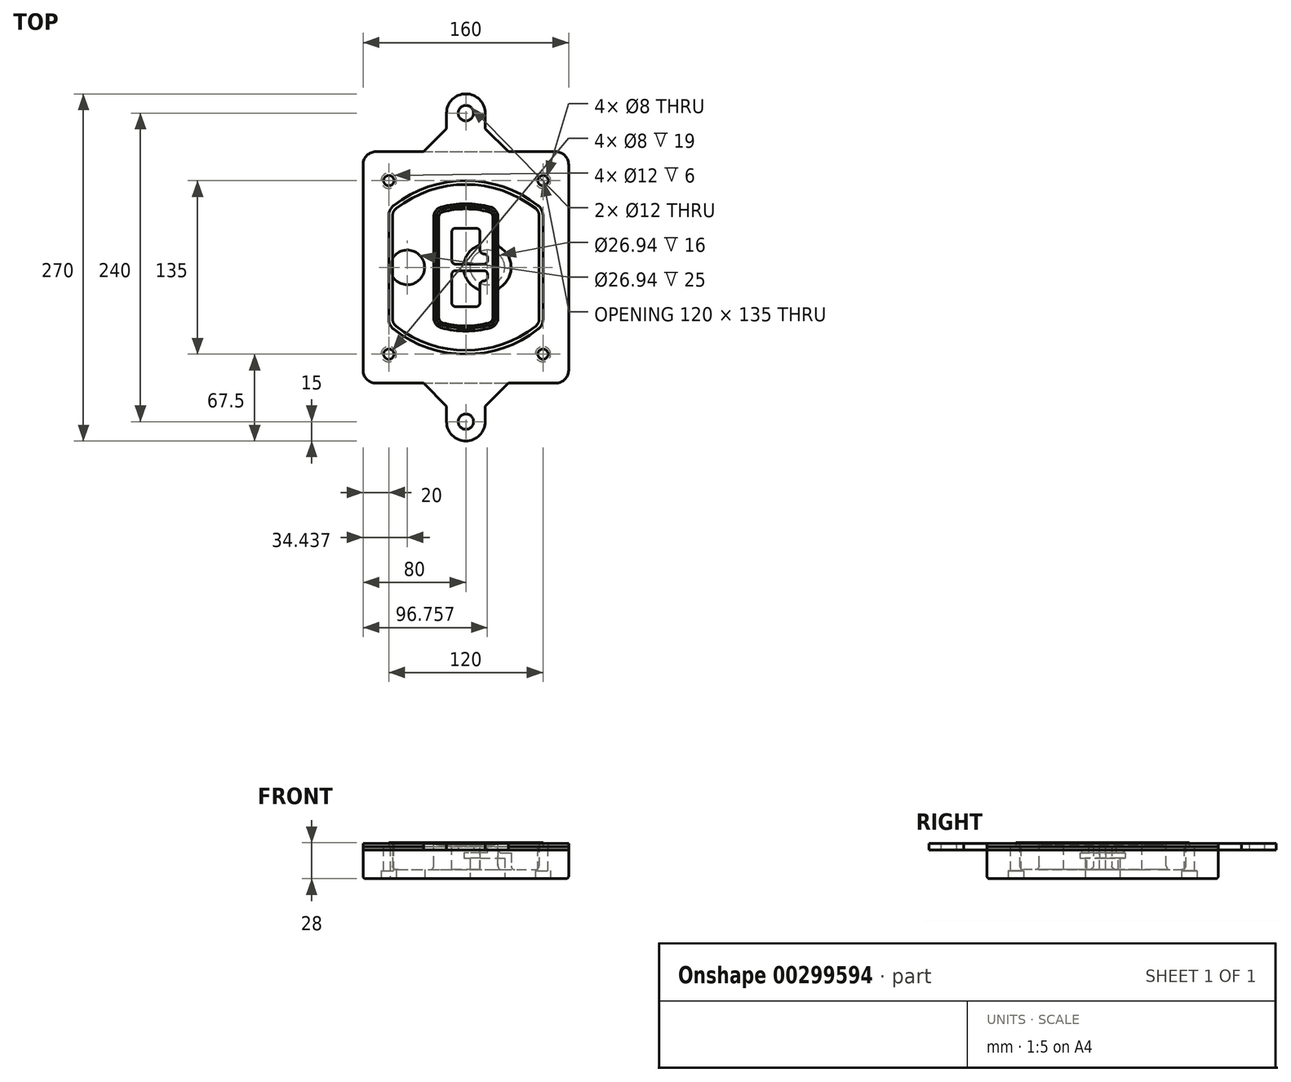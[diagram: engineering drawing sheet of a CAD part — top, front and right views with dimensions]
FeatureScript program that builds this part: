
annotation { "Feature Type Name" : "Feature", "Feature Type Description" : "" }
export const myFeature = defineFeature(function(context is Context, id is Id, definition is map)
    precondition{}
    {
        {
            var Q0;
            Q0=qCreatedBy(makeId("Top.planeOp"),FACE);
            var sketch = newSketch(context, id + "F0", { "sketchPlane" : qUnion([Q0])});
            skPoint(sketch, "E0.rect.middle", {"position": v(0, 0) * mm});
            skLineSegment(sketch, "E1.bottom", {"start": v(-70, -90) * mm, "end": v(70, -90) * mm});
            skLineSegment(sketch, "E1.top", {"start": v(-70, 90) * mm, "end": v(70, 90) * mm});
            skLineSegment(sketch, "E1.left", {"start": v(-80, -80) * mm, "end": v(-80, 80) * mm});
            skLineSegment(sketch, "E1.right", {"start": v(80, -80) * mm, "end": v(80, 80) * mm});
            skLineSegment(sketch, "E2", {"start": v(-80, 90) * mm, "end": v(80, -90) * mm, "construction": true});
            skLineSegment(sketch, "E3", {"start": v(80, 90) * mm, "end": v(-80, -90) * mm, "construction": true});
            skCircle(sketch, "E4", {"center": v(-60, 67.5) * mm, "radius": 4 * mm});
            skCircle(sketch, "E5", {"center": v(60, 67.5) * mm, "radius": 4 * mm});
            skCircle(sketch, "E6", {"center": v(60, -67.5) * mm, "radius": 4 * mm});
            skCircle(sketch, "E7", {"center": v(-60, -67.5) * mm, "radius": 4 * mm});
            skLineSegment(sketch, "E8", {"start": v(-60, 67.5) * mm, "end": v(60, 67.5) * mm, "construction": true});
            skLineSegment(sketch, "E9", {"start": v(60, 67.5) * mm, "end": v(60, -67.5) * mm, "construction": true});
            skLineSegment(sketch, "E10", {"start": v(60, -67.5) * mm, "end": v(-60, -67.5) * mm, "construction": true});
            skLineSegment(sketch, "E11", {"start": v(-60, -67.5) * mm, "end": v(-60, 67.5) * mm, "construction": true});
            skLineSegment(sketch, "E12", {"start": v(-60, 40.3) * mm, "end": v(-60, -40.3) * mm});
            skLineSegment(sketch, "E13", {"start": v(60, 40.3) * mm, "end": v(60, -40.3) * mm});
            skArc(sketch, "E14", {"start": v(56.15, 48.18) * mm, "mid": v(0, 67.5) * mm, "end": v(-56.15, 48.18) * mm});
            skArc(sketch, "E15", {"start": v(-56.15, -48.18) * mm, "mid": v(0, -67.5) * mm, "end": v(56.15, -48.18) * mm});
            skLineSegment(sketch, "E16", {"start": v(-60, 0) * mm, "end": v(60, 0) * mm, "construction": true});
            skPoint(sketch, "E17.visualSharp", {"position": v(-60, -45) * mm});
            skArc(sketch, "E17.filletArc", {"start": v(-60, -40.3) * mm, "mid": v(-58.99, -44.68) * mm, "end": v(-56.15, -48.18) * mm});
            skPoint(sketch, "E18.visualSharp", {"position": v(-60, 45) * mm});
            skArc(sketch, "E18.filletArc", {"start": v(-56.15, 48.18) * mm, "mid": v(-58.99, 44.68) * mm, "end": v(-60, 40.3) * mm});
            skPoint(sketch, "E19.visualSharp", {"position": v(60, 45) * mm});
            skArc(sketch, "E19.filletArc", {"start": v(60, 40.3) * mm, "mid": v(58.99, 44.68) * mm, "end": v(56.15, 48.18) * mm});
            skPoint(sketch, "E20.visualSharp", {"position": v(60, -45) * mm});
            skArc(sketch, "E20.filletArc", {"start": v(56.15, -48.18) * mm, "mid": v(58.99, -44.68) * mm, "end": v(60, -40.3) * mm});
            skPoint(sketch, "E21.visualSharp", {"position": v(-80, 90) * mm});
            skArc(sketch, "E21.filletArc", {"start": v(-70, 90) * mm, "mid": v(-77.07, 87.07) * mm, "end": v(-80, 80) * mm});
            skPoint(sketch, "E22.visualSharp", {"position": v(80, 90) * mm});
            skArc(sketch, "E22.filletArc", {"start": v(80, 80) * mm, "mid": v(77.07, 87.07) * mm, "end": v(70, 90) * mm});
            skPoint(sketch, "E23.visualSharp", {"position": v(80, -90) * mm});
            skArc(sketch, "E23.filletArc", {"start": v(70, -90) * mm, "mid": v(77.07, -87.07) * mm, "end": v(80, -80) * mm});
            skPoint(sketch, "E24.visualSharp", {"position": v(-80, -90) * mm});
            skArc(sketch, "E24.filletArc", {"start": v(-80, -80) * mm, "mid": v(-77.07, -87.07) * mm, "end": v(-70, -90) * mm});
            skArc(sketch, "E25.0", {"start": v(57, 40.3) * mm, "mid": v(56.3, 43.36) * mm, "end": v(54.3, 45.81) * mm});
            skLineSegment(sketch, "E25.1", {"start": v(57, 40.3) * mm, "end": v(57, -40.3) * mm});
            skArc(sketch, "E25.2", {"start": v(54.3, -45.81) * mm, "mid": v(56.3, -43.36) * mm, "end": v(57, -40.3) * mm});
            skArc(sketch, "E25.3", {"start": v(-54.3, -45.81) * mm, "mid": v(0, -64.5) * mm, "end": v(54.3, -45.81) * mm});
            skArc(sketch, "E25.4", {"start": v(-57, -40.3) * mm, "mid": v(-56.3, -43.36) * mm, "end": v(-54.3, -45.81) * mm});
            skArc(sketch, "E25.5", {"start": v(54.3, 45.81) * mm, "mid": v(0, 64.5) * mm, "end": v(-54.3, 45.81) * mm});
            skLineSegment(sketch, "E25.6", {"start": v(-57, 40.3) * mm, "end": v(-57, -40.3) * mm});
            skArc(sketch, "E25.7", {"start": v(-54.3, 45.81) * mm, "mid": v(-56.3, 43.36) * mm, "end": v(-57, 40.3) * mm});
            skArc(sketch, "E26.0", {"start": v(-58.62, 51.33) * mm, "mid": v(-62.58, 46.43) * mm, "end": v(-64, 40.3) * mm});
            skArc(sketch, "E26.1", {"start": v(58.62, 51.33) * mm, "mid": v(0, 71.5) * mm, "end": v(-58.62, 51.33) * mm});
            skArc(sketch, "E26.2", {"start": v(64, 40.3) * mm, "mid": v(62.58, 46.43) * mm, "end": v(58.62, 51.33) * mm});
            skLineSegment(sketch, "E26.3", {"start": v(64, 40.3) * mm, "end": v(64, -40.3) * mm});
            skArc(sketch, "E26.4", {"start": v(58.62, -51.33) * mm, "mid": v(62.58, -46.43) * mm, "end": v(64, -40.3) * mm});
            skLineSegment(sketch, "E26.5", {"start": v(-64, 40.3) * mm, "end": v(-64, -40.3) * mm});
            skArc(sketch, "E26.6", {"start": v(-58.62, -51.33) * mm, "mid": v(0, -71.5) * mm, "end": v(58.62, -51.33) * mm});
            skArc(sketch, "E26.7", {"start": v(-64, -40.3) * mm, "mid": v(-62.58, -46.43) * mm, "end": v(-58.62, -51.33) * mm});
            skSolve(sketch);
        }
        {
            var Q0;
            Q0=makeQuery(id+"F0.imprint","IMPRINT",FACE,{"disambiguationData":[TD([[makeQuery(id+"F0.imprint","IMPRINT",EDGE,{"derivedFrom":sQuery(id+"F0.wireOp",EDGE,"E1.bottom")}),1.0]])]});
            var Q1;
            Q1=makeQuery(id+"F0.imprint","IMPRINT",FACE,{"disambiguationData":[TD([[makeQuery(id+"F0.imprint","IMPRINT",EDGE,{"derivedFrom":sQuery(id+"F0.wireOp",EDGE,"E12")}),1.0]])]});
            var Q2;
            Q2=makeQuery(id+"F0.imprint","IMPRINT",FACE,{"disambiguationData":[TD([[makeQuery(id+"F0.imprint","IMPRINT",EDGE,{"derivedFrom":sQuery(id+"F0.wireOp",EDGE,"E25.0")}),1.0]])]});
            var Q3;
            Q3=makeQuery(id+"F0.imprint","IMPRINT",FACE,{"disambiguationData":[TD([[makeQuery(id+"F0.imprint","IMPRINT",EDGE,{"derivedFrom":sQuery(id+"F0.wireOp",EDGE,"E12")}),-1.0]])]});
            extrude(context, id + "F1", {"entities" : qUnion([Q0, Q1, Q2, Q3]), "oppositeDirection" : true, "depth" : 25 * mm});
        }
        {
            var Q0;
            Q0=makeQuery(id+"F0.imprint","IMPRINT",FACE,{"disambiguationData":[TD([[makeQuery(id+"F0.imprint","IMPRINT",EDGE,{"derivedFrom":sQuery(id+"F0.wireOp",EDGE,"E12")}),1.0]])]});
            extrude(context, id + "F2", {"entities" : qUnion([Q0]), "operationType" : NewBodyOperationType.ADD, "depth" : 3 * mm});
        }
        {
            var Q0;
            Q0=makeQuery(id+"F0.imprint","IMPRINT",FACE,{"disambiguationData":[TD([[makeQuery(id+"F0.imprint","IMPRINT",EDGE,{"derivedFrom":sQuery(id+"F0.wireOp",EDGE,"E25.0")}),1.0]])]});
            extrude(context, id + "F3", {"entities" : qUnion([Q0]), "operationType" : NewBodyOperationType.REMOVE, "oppositeDirection" : true, "depth" : 18 * mm});
        }
        {
            var Q0;
            Q0=makeQuery(id+"F2.opExtrude","CAP_FACE",FACE,{"disambiguationData":[OSD([sQuery(id+"F0.wireOp",EDGE,"E12"),sQuery(id+"F0.wireOp",EDGE,"E13"),sQuery(id+"F0.wireOp",EDGE,"E14"),sQuery(id+"F0.wireOp",EDGE,"E15"),sQuery(id+"F0.wireOp",EDGE,"E17.filletArc"),sQuery(id+"F0.wireOp",EDGE,"E18.filletArc"),sQuery(id+"F0.wireOp",EDGE,"E19.filletArc"),sQuery(id+"F0.wireOp",EDGE,"E20.filletArc"),sQuery(id+"F0.wireOp",EDGE,"E25.0"),sQuery(id+"F0.wireOp",EDGE,"E25.1"),sQuery(id+"F0.wireOp",EDGE,"E25.2"),sQuery(id+"F0.wireOp",EDGE,"E25.3"),sQuery(id+"F0.wireOp",EDGE,"E25.4"),sQuery(id+"F0.wireOp",EDGE,"E25.5"),sQuery(id+"F0.wireOp",EDGE,"E25.6"),sQuery(id+"F0.wireOp",EDGE,"E25.7")])],"isStart":false});
            var sketch = newSketch(context, id + "F4", { "sketchPlane" : qUnion([Q0])});
            skArc(sketch, "E27.0", {"start": v(-19.08, -46.97) * mm, "mid": v(0, -49.5) * mm, "end": v(19.08, -46.97) * mm});
            skArc(sketch, "E28.0", {"start": v(19.08, 46.97) * mm, "mid": v(0, 49.5) * mm, "end": v(-19.08, 46.97) * mm});
            skLineSegment(sketch, "E29", {"start": v(-25, 39.25) * mm, "end": v(-25, -39.25) * mm});
            skLineSegment(sketch, "E30", {"start": v(25, 39.25) * mm, "end": v(25, -39.25) * mm});
            skLineSegment(sketch, "E31", {"start": v(-25, 45.1) * mm, "end": v(25, 45.1) * mm, "construction": true});
            skLineSegment(sketch, "E32", {"start": v(-25, -45.1) * mm, "end": v(25, -45.1) * mm, "construction": true});
            skPoint(sketch, "E33.visualSharp", {"position": v(-25, 45.1) * mm});
            skArc(sketch, "E33.filletArc", {"start": v(-19.08, 46.97) * mm, "mid": v(-23.35, 44.11) * mm, "end": v(-25, 39.25) * mm});
            skPoint(sketch, "E34.visualSharp", {"position": v(25, 45.1) * mm});
            skArc(sketch, "E34.filletArc", {"start": v(25, 39.25) * mm, "mid": v(23.35, 44.11) * mm, "end": v(19.08, 46.97) * mm});
            skPoint(sketch, "E35.visualSharp", {"position": v(25, -45.1) * mm});
            skArc(sketch, "E35.filletArc", {"start": v(19.08, -46.97) * mm, "mid": v(23.35, -44.11) * mm, "end": v(25, -39.25) * mm});
            skPoint(sketch, "E36.visualSharp", {"position": v(-25, -45.1) * mm});
            skArc(sketch, "E36.filletArc", {"start": v(-25, -39.25) * mm, "mid": v(-23.35, -44.11) * mm, "end": v(-19.08, -46.97) * mm});
            skArc(sketch, "E37.0", {"start": v(54.3, 45.81) * mm, "mid": v(0, 64.5) * mm, "end": v(-54.3, 45.81) * mm});
            skArc(sketch, "E37.1", {"start": v(-54.3, 45.81) * mm, "mid": v(-56.3, 43.36) * mm, "end": v(-57, 40.3) * mm});
            skLineSegment(sketch, "E37.2", {"start": v(-57, 40.3) * mm, "end": v(-57, -40.3) * mm});
            skArc(sketch, "E37.3", {"start": v(-57, -40.3) * mm, "mid": v(-56.3, -43.36) * mm, "end": v(-54.3, -45.81) * mm});
            skArc(sketch, "E37.4", {"start": v(-54.3, -45.81) * mm, "mid": v(0, -64.5) * mm, "end": v(54.3, -45.81) * mm});
            skArc(sketch, "E37.5", {"start": v(54.3, -45.81) * mm, "mid": v(56.3, -43.36) * mm, "end": v(57, -40.3) * mm});
            skLineSegment(sketch, "E37.6", {"start": v(57, 40.3) * mm, "end": v(57, -40.3) * mm});
            skArc(sketch, "E37.7", {"start": v(57, 40.3) * mm, "mid": v(56.3, 43.36) * mm, "end": v(54.3, 45.81) * mm});
            skLineSegment(sketch, "E38.0", {"start": v(23, 39.25) * mm, "end": v(23, -39.25) * mm});
            skArc(sketch, "E38.1", {"start": v(18.56, -45.04) * mm, "mid": v(21.76, -42.9) * mm, "end": v(23, -39.25) * mm});
            skArc(sketch, "E38.2", {"start": v(-18.56, -45.04) * mm, "mid": v(0, -47.5) * mm, "end": v(18.56, -45.04) * mm});
            skArc(sketch, "E38.3", {"start": v(-23, -39.25) * mm, "mid": v(-21.76, -42.9) * mm, "end": v(-18.56, -45.04) * mm});
            skLineSegment(sketch, "E38.4", {"start": v(-23, 39.25) * mm, "end": v(-23, -39.25) * mm});
            skArc(sketch, "E38.5", {"start": v(23, 39.25) * mm, "mid": v(21.76, 42.9) * mm, "end": v(18.56, 45.04) * mm});
            skArc(sketch, "E38.6", {"start": v(-18.56, 45.04) * mm, "mid": v(-21.76, 42.9) * mm, "end": v(-23, 39.25) * mm});
            skArc(sketch, "E38.7", {"start": v(18.56, 45.04) * mm, "mid": v(0, 47.5) * mm, "end": v(-18.56, 45.04) * mm});
            skArc(sketch, "E39.0", {"start": v(21, 39.25) * mm, "mid": v(20.18, 41.68) * mm, "end": v(18.04, 43.1) * mm});
            skLineSegment(sketch, "E39.1", {"start": v(21, 39.25) * mm, "end": v(21, -39.25) * mm});
            skArc(sketch, "E39.2", {"start": v(18.04, -43.1) * mm, "mid": v(20.18, -41.68) * mm, "end": v(21, -39.25) * mm});
            skArc(sketch, "E39.3", {"start": v(-18.04, -43.1) * mm, "mid": v(0, -45.5) * mm, "end": v(18.04, -43.1) * mm});
            skArc(sketch, "E39.4", {"start": v(-21, -39.25) * mm, "mid": v(-20.18, -41.68) * mm, "end": v(-18.04, -43.1) * mm});
            skArc(sketch, "E39.5", {"start": v(18.04, 43.1) * mm, "mid": v(0, 45.5) * mm, "end": v(-18.04, 43.1) * mm});
            skLineSegment(sketch, "E39.6", {"start": v(-21, 39.25) * mm, "end": v(-21, -39.25) * mm});
            skArc(sketch, "E39.7", {"start": v(-18.04, 43.1) * mm, "mid": v(-20.18, 41.68) * mm, "end": v(-21, 39.25) * mm});
            skLineSegment(sketch, "E40", {"start": v(-25, 0) * mm, "end": v(25, 0) * mm, "construction": true});
            skLineSegment(sketch, "E41", {"start": v(-11, 5.5) * mm, "end": v(-11, 27.5) * mm});
            skLineSegment(sketch, "E42", {"start": v(-8, 30.5) * mm, "end": v(8, 30.5) * mm});
            skLineSegment(sketch, "E43", {"start": v(11, 27.5) * mm, "end": v(11, 13.5) * mm});
            skLineSegment(sketch, "E44", {"start": v(14, 10.5) * mm, "end": v(14, 10.5) * mm});
            skLineSegment(sketch, "E45", {"start": v(17, 7.5) * mm, "end": v(17, 5.5) * mm});
            skLineSegment(sketch, "E46", {"start": v(14, 2.5) * mm, "end": v(-8, 2.5) * mm});
            skPoint(sketch, "E47.visualSharp", {"position": v(-11, 30.5) * mm});
            skArc(sketch, "E47.filletArc", {"start": v(-8, 30.5) * mm, "mid": v(-10.12, 29.62) * mm, "end": v(-11, 27.5) * mm});
            skPoint(sketch, "E48.visualSharp", {"position": v(11, 30.5) * mm});
            skArc(sketch, "E48.filletArc", {"start": v(11, 27.5) * mm, "mid": v(10.12, 29.62) * mm, "end": v(8, 30.5) * mm});
            skPoint(sketch, "E49.visualSharp", {"position": v(11, 10.5) * mm});
            skArc(sketch, "E49.filletArc", {"start": v(11, 13.5) * mm, "mid": v(11.88, 11.38) * mm, "end": v(14, 10.5) * mm});
            skPoint(sketch, "E50.visualSharp", {"position": v(17, 10.5) * mm});
            skArc(sketch, "E50.filletArc", {"start": v(17, 7.5) * mm, "mid": v(16.12, 9.62) * mm, "end": v(14, 10.5) * mm});
            skPoint(sketch, "E51.visualSharp", {"position": v(17, 2.5) * mm});
            skArc(sketch, "E51.filletArc", {"start": v(14, 2.5) * mm, "mid": v(16.12, 3.38) * mm, "end": v(17, 5.5) * mm});
            skPoint(sketch, "E52.visualSharp", {"position": v(-11, 2.5) * mm});
            skArc(sketch, "E52.filletArc", {"start": v(-11, 5.5) * mm, "mid": v(-10.12, 3.38) * mm, "end": v(-8, 2.5) * mm});
            skLineSegment(sketch, "E53.0.MirrorCS", {"start": v(14, -2.5) * mm, "end": v(-8, -2.5) * mm});
            skArc(sketch, "E54.0.MirrorCS", {"start": v(-11, -5.5) * mm, "mid": v(-10.12, -3.38) * mm, "end": v(-8, -2.5) * mm});
            skLineSegment(sketch, "E55.0.MirrorCS", {"start": v(-11, -5.5) * mm, "end": v(-11, -27.5) * mm});
            skArc(sketch, "E56.0.MirrorCS", {"start": v(-8, -30.5) * mm, "mid": v(-10.12, -29.62) * mm, "end": v(-11, -27.5) * mm});
            skLineSegment(sketch, "E57.0.MirrorCS", {"start": v(-8, -30.5) * mm, "end": v(8, -30.5) * mm});
            skArc(sketch, "E58.0.MirrorCS", {"start": v(11, -27.5) * mm, "mid": v(10.12, -29.62) * mm, "end": v(8, -30.5) * mm});
            skLineSegment(sketch, "E59.0.MirrorCS", {"start": v(11, -27.5) * mm, "end": v(11, -13.5) * mm});
            skArc(sketch, "E60.0.MirrorCS", {"start": v(11, -13.5) * mm, "mid": v(11.88, -11.38) * mm, "end": v(14, -10.5) * mm});
            skArc(sketch, "E61.0.MirrorCS", {"start": v(17, -7.5) * mm, "mid": v(16.12, -9.62) * mm, "end": v(14, -10.5) * mm});
            skLineSegment(sketch, "E62.0.MirrorCS", {"start": v(17, -7.5) * mm, "end": v(17, -5.5) * mm});
            skArc(sketch, "E63.0.MirrorCS", {"start": v(14, -2.5) * mm, "mid": v(16.12, -3.38) * mm, "end": v(17, -5.5) * mm});
            skSolve(sketch);
        }
        {
            var Q0;
            Q0=makeQuery(id+"F4.imprint","IMPRINT",FACE,{"disambiguationData":[TD([[makeQuery(id+"F4.imprint","IMPRINT",EDGE,{"derivedFrom":sQuery(id+"F4.wireOp",EDGE,"E27.0")}),1.0]])]});
            var Q1;
            Q1=makeQuery(id+"F4.imprint","IMPRINT",FACE,{"disambiguationData":[TD([[makeQuery(id+"F4.imprint","IMPRINT",EDGE,{"derivedFrom":sQuery(id+"F4.wireOp",EDGE,"E38.0")}),-1.0]])]});
            var Q2;
            Q2=makeQuery(id+"F4.imprint","IMPRINT",FACE,{"disambiguationData":[TD([[makeQuery(id+"F4.imprint","IMPRINT",EDGE,{"derivedFrom":sQuery(id+"F4.wireOp",EDGE,"E39.0")}),1.0]])]});
            extrude(context, id + "F5", {"entities" : qUnion([Q0, Q1, Q2]), "operationType" : NewBodyOperationType.ADD, "endBound" : BoundingType.UP_TO_NEXT, "oppositeDirection" : true, "depth" : 25 * mm});
        }
        {
            var Q0;
            Q0=makeQuery(id+"F4.imprint","IMPRINT",FACE,{"disambiguationData":[TD([[makeQuery(id+"F4.imprint","IMPRINT",EDGE,{"derivedFrom":sQuery(id+"F4.wireOp",EDGE,"E38.0")}),-1.0]])]});
            extrude(context, id + "F6", {"entities" : qUnion([Q0]), "operationType" : NewBodyOperationType.REMOVE, "oppositeDirection" : true, "depth" : 2 * mm});
        }
        {
            var Q0;
            Q0=makeQuery(id+"F1.opExtrude","CAP_FACE",FACE,{"disambiguationData":[OSD([sQuery(id+"F0.wireOp",EDGE,"E1.bottom"),sQuery(id+"F0.wireOp",EDGE,"E1.top"),sQuery(id+"F0.wireOp",EDGE,"E1.left"),sQuery(id+"F0.wireOp",EDGE,"E1.right"),sQuery(id+"F0.wireOp",EDGE,"E4"),sQuery(id+"F0.wireOp",EDGE,"E5"),sQuery(id+"F0.wireOp",EDGE,"E6"),sQuery(id+"F0.wireOp",EDGE,"E7"),sQuery(id+"F0.wireOp",EDGE,"E21.filletArc"),sQuery(id+"F0.wireOp",EDGE,"E22.filletArc"),sQuery(id+"F0.wireOp",EDGE,"E23.filletArc"),sQuery(id+"F0.wireOp",EDGE,"E24.filletArc")])],"isStart":false});
            var sketch = newSketch(context, id + "F7", { "sketchPlane" : qUnion([Q0])});
            skCircle(sketch, "E64", {"center": v(16.76, 0) * mm, "radius": 13.47 * mm});
            skCircle(sketch, "E65", {"center": v(-45.56, 0) * mm, "radius": 13.47 * mm});
            skLineSegment(sketch, "E66", {"start": v(80, 0) * mm, "end": v(-80, 0) * mm});
            skCircle(sketch, "E67", {"center": v(16.76, 0) * mm, "radius": 18.47 * mm});
            skCircle(sketch, "E68", {"center": v(60, -67.5) * mm, "radius": 6 * mm});
            skCircle(sketch, "E69", {"center": v(-60, -67.5) * mm, "radius": 6 * mm});
            skCircle(sketch, "E70", {"center": v(-60, 67.5) * mm, "radius": 6 * mm});
            skCircle(sketch, "E71", {"center": v(60, 67.5) * mm, "radius": 6 * mm});
            skSolve(sketch);
        }
        {
            var Q0;
            {var subQ1=sQuery(id+"F7.wireOp",EDGE,"E66");var subQ4=sQuery(id+"F7.wireOp",EDGE,"E64");var subQ6=makeQuery(id+"F7.imprint","INTERSECT",VERTEX,{"disambiguationData":[OD(0.0)],"derivedFrom":[subQ4,subQ1]});Q0=makeQuery(id+"F7.imprint","IMPRINT",FACE,{"disambiguationData":[TD([[makeQuery(id+"F7.imprint","IMPRINT",EDGE,{"disambiguationData":[TD([[subQ6,-1.0]])],"derivedFrom":subQ4}),-1.0]])]});}
            var Q1;
            {var subQ0=sQuery(id+"F7.wireOp",EDGE,"E66");var subQ1=sQuery(id+"F7.wireOp",EDGE,"E64");var subQ3=makeQuery(id+"F7.imprint","INTERSECT",VERTEX,{"disambiguationData":[OD(0.0)],"derivedFrom":[subQ1,subQ0]});Q1=makeQuery(id+"F7.imprint","IMPRINT",FACE,{"disambiguationData":[TD([[makeQuery(id+"F7.imprint","IMPRINT",EDGE,{"disambiguationData":[TD([[subQ3,-1.0]])],"derivedFrom":subQ1}),1.0]])]});}
            var Q2;
            {var subQ0=sQuery(id+"F7.wireOp",EDGE,"E66");var subQ1=sQuery(id+"F7.wireOp",EDGE,"E64");var subQ3=makeQuery(id+"F7.imprint","INTERSECT",VERTEX,{"disambiguationData":[OD(0.0)],"derivedFrom":[subQ1,subQ0]});Q2=makeQuery(id+"F7.imprint","IMPRINT",FACE,{"disambiguationData":[TD([[makeQuery(id+"F7.imprint","IMPRINT",EDGE,{"disambiguationData":[TD([[subQ3,1.0]])],"derivedFrom":subQ1}),1.0]])]});}
            var Q3;
            {var subQ1=sQuery(id+"F7.wireOp",EDGE,"E66");var subQ4=sQuery(id+"F7.wireOp",EDGE,"E64");var subQ6=makeQuery(id+"F7.imprint","INTERSECT",VERTEX,{"disambiguationData":[OD(0.0)],"derivedFrom":[subQ4,subQ1]});Q3=makeQuery(id+"F7.imprint","IMPRINT",FACE,{"disambiguationData":[TD([[makeQuery(id+"F7.imprint","IMPRINT",EDGE,{"disambiguationData":[TD([[subQ6,1.0]])],"derivedFrom":subQ4}),-1.0]])]});}
            extrude(context, id + "F8", {"entities" : qUnion([Q0, Q1, Q2, Q3]), "operationType" : NewBodyOperationType.ADD, "oppositeDirection" : true, "depth" : 20 * mm});
        }
        {
            var Q0;
            {var subQ0=sQuery(id+"F7.wireOp",EDGE,"E66");var subQ1=sQuery(id+"F7.wireOp",EDGE,"E64");var subQ3=makeQuery(id+"F7.imprint","INTERSECT",VERTEX,{"disambiguationData":[OD(0.0)],"derivedFrom":[subQ1,subQ0]});Q0=makeQuery(id+"F7.imprint","IMPRINT",FACE,{"disambiguationData":[TD([[makeQuery(id+"F7.imprint","IMPRINT",EDGE,{"disambiguationData":[TD([[subQ3,-1.0]])],"derivedFrom":subQ1}),1.0]])]});}
            var Q1;
            {var subQ0=sQuery(id+"F7.wireOp",EDGE,"E66");var subQ1=sQuery(id+"F7.wireOp",EDGE,"E64");var subQ3=makeQuery(id+"F7.imprint","INTERSECT",VERTEX,{"disambiguationData":[OD(0.0)],"derivedFrom":[subQ1,subQ0]});Q1=makeQuery(id+"F7.imprint","IMPRINT",FACE,{"disambiguationData":[TD([[makeQuery(id+"F7.imprint","IMPRINT",EDGE,{"disambiguationData":[TD([[subQ3,1.0]])],"derivedFrom":subQ1}),1.0]])]});}
            extrude(context, id + "F9", {"entities" : qUnion([Q0, Q1]), "operationType" : NewBodyOperationType.REMOVE, "oppositeDirection" : true, "depth" : 16 * mm});
        }
        {
            var Q0;
            {var subQ0=sQuery(id+"F7.wireOp",EDGE,"E66");var subQ1=sQuery(id+"F7.wireOp",EDGE,"E65");var subQ3=makeQuery(id+"F7.imprint","INTERSECT",VERTEX,{"disambiguationData":[OD(0.0)],"derivedFrom":[subQ1,subQ0]});Q0=makeQuery(id+"F7.imprint","IMPRINT",FACE,{"disambiguationData":[TD([[makeQuery(id+"F7.imprint","IMPRINT",EDGE,{"disambiguationData":[TD([[subQ3,-1.0]])],"derivedFrom":subQ1}),1.0]])]});}
            var Q1;
            {var subQ0=sQuery(id+"F7.wireOp",EDGE,"E66");var subQ1=sQuery(id+"F7.wireOp",EDGE,"E65");var subQ3=makeQuery(id+"F7.imprint","INTERSECT",VERTEX,{"disambiguationData":[OD(0.0)],"derivedFrom":[subQ1,subQ0]});Q1=makeQuery(id+"F7.imprint","IMPRINT",FACE,{"disambiguationData":[TD([[makeQuery(id+"F7.imprint","IMPRINT",EDGE,{"disambiguationData":[TD([[subQ3,1.0]])],"derivedFrom":subQ1}),1.0]])]});}
            extrude(context, id + "F10", {"entities" : qUnion([Q0, Q1]), "operationType" : NewBodyOperationType.REMOVE, "oppositeDirection" : true, "depth" : 25 * mm});
        }
        {
            var Q0;
            Q0=makeQuery(id+"F7.imprint","IMPRINT",FACE,{"disambiguationData":[TD([[makeQuery(id+"F7.imprint","IMPRINT",EDGE,{"derivedFrom":sQuery(id+"F7.wireOp",EDGE,"E68")}),1.0]])]});
            var Q1;
            Q1=makeQuery(id+"F7.imprint","IMPRINT",FACE,{"disambiguationData":[TD([[makeQuery(id+"F7.imprint","IMPRINT",EDGE,{"derivedFrom":makeQuery(id+"F1.opExtrude","CAP_EDGE",EDGE,{"disambiguationData":[OSD([sQuery(id+"F0.wireOp",EDGE,"E5")])],"isStart":false})}),-1.0]])]});
            var Q2;
            Q2=makeQuery(id+"F7.imprint","IMPRINT",FACE,{"disambiguationData":[TD([[makeQuery(id+"F7.imprint","IMPRINT",EDGE,{"derivedFrom":sQuery(id+"F7.wireOp",EDGE,"E69")}),1.0]])]});
            var Q3;
            Q3=makeQuery(id+"F7.imprint","IMPRINT",FACE,{"disambiguationData":[TD([[makeQuery(id+"F7.imprint","IMPRINT",EDGE,{"derivedFrom":makeQuery(id+"F1.opExtrude","CAP_EDGE",EDGE,{"disambiguationData":[OSD([sQuery(id+"F0.wireOp",EDGE,"E4")])],"isStart":false})}),-1.0]])]});
            var Q4;
            Q4=makeQuery(id+"F7.imprint","IMPRINT",FACE,{"disambiguationData":[TD([[makeQuery(id+"F7.imprint","IMPRINT",EDGE,{"derivedFrom":sQuery(id+"F7.wireOp",EDGE,"E70")}),1.0]])]});
            var Q5;
            Q5=makeQuery(id+"F7.imprint","IMPRINT",FACE,{"disambiguationData":[TD([[makeQuery(id+"F7.imprint","IMPRINT",EDGE,{"derivedFrom":makeQuery(id+"F1.opExtrude","CAP_EDGE",EDGE,{"disambiguationData":[OSD([sQuery(id+"F0.wireOp",EDGE,"E7")])],"isStart":false})}),-1.0]])]});
            var Q6;
            Q6=makeQuery(id+"F7.imprint","IMPRINT",FACE,{"disambiguationData":[TD([[makeQuery(id+"F7.imprint","IMPRINT",EDGE,{"derivedFrom":sQuery(id+"F7.wireOp",EDGE,"E71")}),1.0]])]});
            var Q7;
            Q7=makeQuery(id+"F7.imprint","IMPRINT",FACE,{"disambiguationData":[TD([[makeQuery(id+"F7.imprint","IMPRINT",EDGE,{"derivedFrom":makeQuery(id+"F1.opExtrude","CAP_EDGE",EDGE,{"disambiguationData":[OSD([sQuery(id+"F0.wireOp",EDGE,"E6")])],"isStart":false})}),-1.0]])]});
            extrude(context, id + "F11", {"entities" : qUnion([Q0, Q1, Q2, Q3, Q4, Q5, Q6, Q7]), "operationType" : NewBodyOperationType.REMOVE, "oppositeDirection" : true, "depth" : 6 * mm});
        }
        {
            var Q0;
            Q0=makeQuery(id+"F9.boolean.opBoolean","COPY",FACE,{"derivedFrom":makeQuery(id+"F9.opExtrude","CAP_FACE",FACE,{"disambiguationData":[OSD([sQuery(id+"F7.wireOp",EDGE,"E64")])],"isStart":false})});
            var sketch = newSketch(context, id + "F12", { "sketchPlane" : qUnion([Q0])});
            skArc(sketch, "E72.0", {"start": v(11, 17.55) * mm, "mid": v(2.57, 11.82) * mm, "end": v(-1.54, 2.5) * mm});
            skArc(sketch, "E72.1", {"start": v(-1.54, -2.5) * mm, "mid": v(2.57, -11.82) * mm, "end": v(11, -17.55) * mm});
            skLineSegment(sketch, "E73", {"start": v(-1.54, -2.5) * mm, "end": v(14, -2.5) * mm});
            skLineSegment(sketch, "E74.0", {"start": v(14, 2.5) * mm, "end": v(-1.54, 2.5) * mm});
            skArc(sketch, "E74.1", {"start": v(14, 2.5) * mm, "mid": v(16.12, 3.38) * mm, "end": v(17, 5.5) * mm});
            skLineSegment(sketch, "E74.2", {"start": v(17, 7.5) * mm, "end": v(17, 5.5) * mm});
            skArc(sketch, "E74.3", {"start": v(17, 7.5) * mm, "mid": v(16.12, 9.62) * mm, "end": v(14, 10.5) * mm});
            skArc(sketch, "E74.4", {"start": v(11, 13.5) * mm, "mid": v(11.88, 11.38) * mm, "end": v(14, 10.5) * mm});
            skLineSegment(sketch, "E74.5", {"start": v(11, 17.55) * mm, "end": v(11, 13.5) * mm});
            skLineSegment(sketch, "E74.7", {"start": v(14, -2.5) * mm, "end": v(-1.54, -2.5) * mm});
            skArc(sketch, "E74.8", {"start": v(14, -2.5) * mm, "mid": v(16.12, -3.38) * mm, "end": v(17, -5.5) * mm});
            skLineSegment(sketch, "E74.9", {"start": v(17, -7.5) * mm, "end": v(17, -5.5) * mm});
            skArc(sketch, "E74.10", {"start": v(17, -7.5) * mm, "mid": v(16.12, -9.62) * mm, "end": v(14, -10.5) * mm});
            skArc(sketch, "E74.11", {"start": v(11, -13.5) * mm, "mid": v(11.88, -11.38) * mm, "end": v(14, -10.5) * mm});
            skLineSegment(sketch, "E74.12", {"start": v(11, -17.55) * mm, "end": v(11, -13.5) * mm});
            skPoint(sketch, "E75.orphan", {"position": v(11, -27.5) * mm});
            skPoint(sketch, "E76.orphan", {"position": v(-8, -2.5) * mm});
            skPoint(sketch, "E77.orphan", {"position": v(-8, 2.5) * mm});
            skPoint(sketch, "E78.orphan", {"position": v(11, 27.5) * mm});
            skSolve(sketch);
        }
        {
            var Q0;
            {var subQ7=sQuery(id+"F12.wireOp",EDGE,"E72.0");var subQ14=sQuery(id+"F12.wireOp",EDGE,"E72.1");var subQ16=sQuery(id+"F12.wireOp",EDGE,"E74.1");var subQ18=sQuery(id+"F12.wireOp",EDGE,"E74.8");Q0=qUnion([makeQuery(id+"F12.imprint","IMPRINT",FACE,{"disambiguationData":[TD([[makeQuery(id+"F12.imprint","IMPRINT",EDGE,{"derivedFrom":subQ7}),1.0]])]}),makeQuery(id+"F12.imprint","IMPRINT",FACE,{"disambiguationData":[TD([[makeQuery(id+"F12.imprint","IMPRINT",EDGE,{"derivedFrom":subQ14}),1.0]])]}),makeQuery(id+"F12.imprint","IMPRINT",FACE,{"disambiguationData":[TD([[makeQuery(id+"F12.imprint","IMPRINT",EDGE,{"derivedFrom":subQ16}),1.0]])]}),makeQuery(id+"F12.imprint","IMPRINT",FACE,{"disambiguationData":[TD([[makeQuery(id+"F12.imprint","IMPRINT",EDGE,{"derivedFrom":subQ18}),-1.0]])]})]);}
            var Q1;
            Q1=makeQuery(id+"F5.boolean.opBoolean","SPLIT",FACE,{"disambiguationData":[TD([makeQuery(id+"F5.opExtrude","SWEPT_FACE",FACE,{"disambiguationData":[OSD([sQuery(id+"F4.wireOp",EDGE,"E41")])]})])],"derivedFrom":makeQuery(id+"F3.boolean.opBoolean","COPY",FACE,{"derivedFrom":makeQuery(id+"F3.opExtrude","CAP_FACE",FACE,{"disambiguationData":[OSD([sQuery(id+"F0.wireOp",EDGE,"E25.0"),sQuery(id+"F0.wireOp",EDGE,"E25.1"),sQuery(id+"F0.wireOp",EDGE,"E25.2"),sQuery(id+"F0.wireOp",EDGE,"E25.3"),sQuery(id+"F0.wireOp",EDGE,"E25.4"),sQuery(id+"F0.wireOp",EDGE,"E25.5"),sQuery(id+"F0.wireOp",EDGE,"E25.6"),sQuery(id+"F0.wireOp",EDGE,"E25.7")])],"isStart":false})})});
            extrude(context, id + "F13", {"entities" : qUnion([Q0]), "operationType" : NewBodyOperationType.REMOVE, "endBound" : BoundingType.UP_TO_SURFACE, "endBoundEntityFace" : qUnion([Q1]), "depth" : 25 * mm});
        }
        {
            var Q0;
            Q0=makeQuery(id+"F3.boolean.opBoolean","COPY",EDGE,{"derivedFrom":makeQuery(id+"F3.opExtrude","CAP_EDGE",EDGE,{"disambiguationData":[OSD([sQuery(id+"F0.wireOp",EDGE,"E25.6")])],"isStart":false})});
            var Q1;
            Q1=makeQuery(id+"F8.boolean.opBoolean","INTERSECT",EDGE,{"derivedFrom":[makeQuery(id+"F5.opExtrude","SWEPT_FACE",FACE,{"disambiguationData":[OSD([sQuery(id+"F4.wireOp",EDGE,"E30")])]}),makeQuery(id+"F8.opExtrude","CAP_FACE",FACE,{"disambiguationData":[OSD([sQuery(id+"F7.wireOp",EDGE,"E67")])],"isStart":false})]});
            var Q2;
            Q2=makeQuery(id+"F8.boolean.opBoolean","INTERSECT",EDGE,{"disambiguationData":[OD(1.0)],"derivedFrom":[makeQuery(id+"F5.opExtrude","SWEPT_FACE",FACE,{"disambiguationData":[OSD([sQuery(id+"F4.wireOp",EDGE,"E30")])]}),makeQuery(id+"F8.opExtrude","SWEPT_FACE",FACE,{"disambiguationData":[OSD([sQuery(id+"F7.wireOp",EDGE,"E67")])]})]});
            var Q3;
            {var subQ0=sQuery(id+"F4.wireOp",EDGE,"E30");Q3=makeQuery(id+"F8.boolean.opBoolean","SPLIT",EDGE,{"disambiguationData":[TD([makeQuery(id+"F5.opExtrude","SWEPT_FACE",FACE,{"disambiguationData":[OSD([sQuery(id+"F4.wireOp",EDGE,"E35.filletArc")])]})])],"derivedFrom":makeQuery(id+"F5.opExtrude","CAP_EDGE",EDGE,{"disambiguationData":[OSD([subQ0])],"isStart":false})});}
            var Q4;
            {var subQ0=sQuery(id+"F0.wireOp",EDGE,"E25.7");var subQ1=sQuery(id+"F0.wireOp",EDGE,"E25.1");var subQ2=sQuery(id+"F0.wireOp",EDGE,"E25.6");var subQ3=sQuery(id+"F0.wireOp",EDGE,"E25.5");var subQ4=sQuery(id+"F0.wireOp",EDGE,"E25.4");var subQ5=sQuery(id+"F0.wireOp",EDGE,"E25.0");var subQ6=sQuery(id+"F0.wireOp",EDGE,"E25.2");var subQ7=sQuery(id+"F0.wireOp",EDGE,"E25.3");Q4=makeQuery(id+"F8.boolean.opBoolean","INTERSECT",EDGE,{"derivedFrom":[makeQuery(id+"F5.boolean.opBoolean","SPLIT",FACE,{"disambiguationData":[TD([makeQuery(id+"F2.opExtrude","SWEPT_FACE",FACE,{"disambiguationData":[OSD([subQ5])]})])],"derivedFrom":makeQuery(id+"F3.boolean.opBoolean","COPY",FACE,{"derivedFrom":makeQuery(id+"F3.opExtrude","CAP_FACE",FACE,{"disambiguationData":[OSD([subQ5,subQ1,subQ6,subQ7,subQ4,subQ3,subQ2,subQ0])],"isStart":false})})}),makeQuery(id+"F8.opExtrude","SWEPT_FACE",FACE,{"disambiguationData":[OSD([sQuery(id+"F7.wireOp",EDGE,"E67")])]})]});}
            var Q5;
            Q5=makeQuery(id+"F8.boolean.opBoolean","INTERSECT",EDGE,{"disambiguationData":[OD(0.0)],"derivedFrom":[makeQuery(id+"F5.opExtrude","SWEPT_FACE",FACE,{"disambiguationData":[OSD([sQuery(id+"F4.wireOp",EDGE,"E30")])]}),makeQuery(id+"F8.opExtrude","SWEPT_FACE",FACE,{"disambiguationData":[OSD([sQuery(id+"F7.wireOp",EDGE,"E67")])]})]});
            fillet(context, id + "F14", {"entities" : qUnion([Q0, Q1, Q2, Q3, Q4, Q5]), "radius" : 3 * mm, "tangentPropagation" : true, "allowEdgeOverflow" : false});
        }
        {
            var Q0;
            Q0=makeQuery(id+"F1.opExtrude","CAP_EDGE",EDGE,{"disambiguationData":[OSD([sQuery(id+"F0.wireOp",EDGE,"E1.bottom")])],"isStart":false});
            fillet(context, id + "F15", {"entities" : qUnion([Q0]), "radius" : 2 * mm, "tangentPropagation" : true, "allowEdgeOverflow" : false});
        }
        {
            var Q0;
            {var subQ0=sQuery(id+"F0.wireOp",EDGE,"E21.filletArc");var subQ1=sQuery(id+"F0.wireOp",EDGE,"E7");var subQ2=sQuery(id+"F0.wireOp",EDGE,"E6");var subQ3=sQuery(id+"F0.wireOp",EDGE,"E5");var subQ4=sQuery(id+"F0.wireOp",EDGE,"E4");var subQ5=sQuery(id+"F0.wireOp",EDGE,"E22.filletArc");var subQ6=sQuery(id+"F0.wireOp",EDGE,"E1.bottom");var subQ7=sQuery(id+"F0.wireOp",EDGE,"E1.right");var subQ8=sQuery(id+"F0.wireOp",EDGE,"E1.top");var subQ9=sQuery(id+"F0.wireOp",EDGE,"E1.left");var subQ10=sQuery(id+"F0.wireOp",EDGE,"E23.filletArc");var subQ11=sQuery(id+"F0.wireOp",EDGE,"E24.filletArc");Q0=makeQuery(id+"F2.boolean.opBoolean","SPLIT",FACE,{"disambiguationData":[TD([makeQuery(id+"F1.opExtrude","SWEPT_FACE",FACE,{"disambiguationData":[OSD([subQ6])]})])],"derivedFrom":makeQuery(id+"F1.opExtrude","CAP_FACE",FACE,{"disambiguationData":[OSD([subQ6,subQ8,subQ9,subQ7,subQ4,subQ3,subQ2,subQ1,subQ0,subQ5,subQ10,subQ11])],"isStart":true})});}
            var sketch = newSketch(context, id + "F16", { "sketchPlane" : qUnion([Q0])});
            skLineSegment(sketch, "E79", {"start": v(0, 90) * mm, "end": v(0, 120) * mm, "construction": true});
            skPoint(sketch, "E79.endSnap0", {"position": v(0, 90) * mm});
            skCircle(sketch, "E80", {"center": v(0, 120) * mm, "radius": 6 * mm});
            skArc(sketch, "E81", {"start": v(15, 120) * mm, "mid": v(0, 135) * mm, "end": v(-15, 120) * mm});
            skLineSegment(sketch, "E82", {"start": v(-15, 120) * mm, "end": v(-15, 108) * mm});
            skLineSegment(sketch, "E83", {"start": v(-15, 108) * mm, "end": v(-33, 90) * mm});
            skLineSegment(sketch, "E84", {"start": v(15, 120) * mm, "end": v(15, 108) * mm});
            skLineSegment(sketch, "E85", {"start": v(15, 108) * mm, "end": v(33, 90) * mm});
            skLineSegment(sketch, "E86", {"start": v(-80, 0) * mm, "end": v(80, 0) * mm, "construction": true});
            skLineSegment(sketch, "E87.MirrorCS", {"start": v(15, -108) * mm, "end": v(33, -90) * mm});
            skLineSegment(sketch, "E88.MirrorCS", {"start": v(15, -120) * mm, "end": v(15, -108) * mm});
            skArc(sketch, "E89.MirrorCS", {"start": v(15, -120) * mm, "mid": v(0, -135) * mm, "end": v(-15, -120) * mm});
            skLineSegment(sketch, "E90.MirrorCS", {"start": v(-15, -120) * mm, "end": v(-15, -108) * mm});
            skCircle(sketch, "E91.MirrorC", {"center": v(0, -120) * mm, "radius": 6 * mm});
            skLineSegment(sketch, "E92.MirrorCS", {"start": v(-15, -108) * mm, "end": v(-33, -90) * mm});
            skLineSegment(sketch, "E93.MirrorCS", {"start": v(0, -90) * mm, "end": v(0, -120) * mm, "construction": true});
            skSolve(sketch);
        }
        {
            var Q0;
            Q0=makeQuery(id+"F16.imprint","IMPRINT",FACE,{"disambiguationData":[TD([[makeQuery(id+"F16.imprint","IMPRINT",EDGE,{"derivedFrom":sQuery(id+"F16.wireOp",EDGE,"E80")}),-1.0]])]});
            var Q1;
            Q1=makeQuery(id+"F16.imprint","IMPRINT",FACE,{"disambiguationData":[TD([[makeQuery(id+"F16.imprint","IMPRINT",EDGE,{"derivedFrom":makeQuery(id+"F1.opExtrude","CAP_EDGE",EDGE,{"disambiguationData":[OSD([sQuery(id+"F0.wireOp",EDGE,"E1.left")])],"isStart":true})}),-1.0]])]});
            var Q2;
            {var subQ0=sQuery(id+"F16.wireOp",EDGE,"E87.MirrorCS");Q2=makeQuery(id+"F16.imprint","IMPRINT",FACE,{"disambiguationData":[TD([[makeQuery(id+"F16.imprint","IMPRINT",EDGE,{"derivedFrom":subQ0}),1.0]])]});}
            extrude(context, id + "F17", {"entities" : qUnion([Q0, Q1, Q2]), "endBound" : BoundingType.SYMMETRIC, "depth" : 5 * mm});
        }
    });
